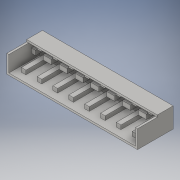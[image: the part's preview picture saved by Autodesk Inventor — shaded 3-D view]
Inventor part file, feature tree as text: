
AUTODESK INVENTOR PART (.ipt)
format: ipt  version: 2016 (Build 200138000, 138)  size: 365,056 bytes
history: native  units: in
note: dims shown in document units (in); Inventor stores cm internally (conversion verified against a paired STEP export)
features: projected_geometry x11, sketch x7, extrude x6
ambient origin geometry x8: Origin, YZ Plane, XZ Plane, XY Plane, X Axis, Y Axis, Z Axis, Center Point
bodies: Solid1 (feature_tree)
feature tree (24):
  extrude  "Extrusion1"  Depth=0.8in
  extrude  "Extrusion2"  Depth=0.23in
  sketch  "Sketch3"  dims[d4=0.25in d5=0.0in d8=0.3937in]
  extrude  "Extrusion3"  Depth=0.3937in
  extrude  "Extrusion4"  Depth=3.1496in
  extrude  "Extrusion5"  Depth=0.1in
  extrude  "Extrusion6"  Depth=0.9843in TaperAngle=0.0deg
  sketch  "Sketch1"  dims[d0=6.2992in d1=0.8in]
  sketch  "Sketch2"  dims[d2=0.4in d3=0.23in]
  sketch  "Sketch4"  dims[d9=1.5748in d11=360.0deg d13=3.1496in d15=0.7874in d16=0.3937in d18=1.0in]
  projected_geometry  "Projected Loop1"
  sketch  "Sketch5"  dims[d20=0.3937in d21=0.0in d22=0.1in]
  projected_geometry  "Projected Loop2"
  sketch  "Sketch6"  dims[d23=0.7874in d24=0.0in d25=0.9843in d26=0.0in]
  projected_geometry  "Projected Loop3"
  projected_geometry  "Projected Loop4"
  projected_geometry  "Projected Loop5"
  projected_geometry  "Projected Loop6"
  projected_geometry  "Projected Loop7"
  projected_geometry  "Projected Loop8"
  projected_geometry  "Projected Loop9"
  projected_geometry  "Projected Loop10"
  sketch  "Sketch7"  dims[d27=0.7874in d28=0.0in d29=0.25in d30=0.5in d31=3.1496in d33=0.7874in d34=0.3937in d36=1.0in d38=3.0in d39=0.0in]
  projected_geometry  "Projected Loop11"
